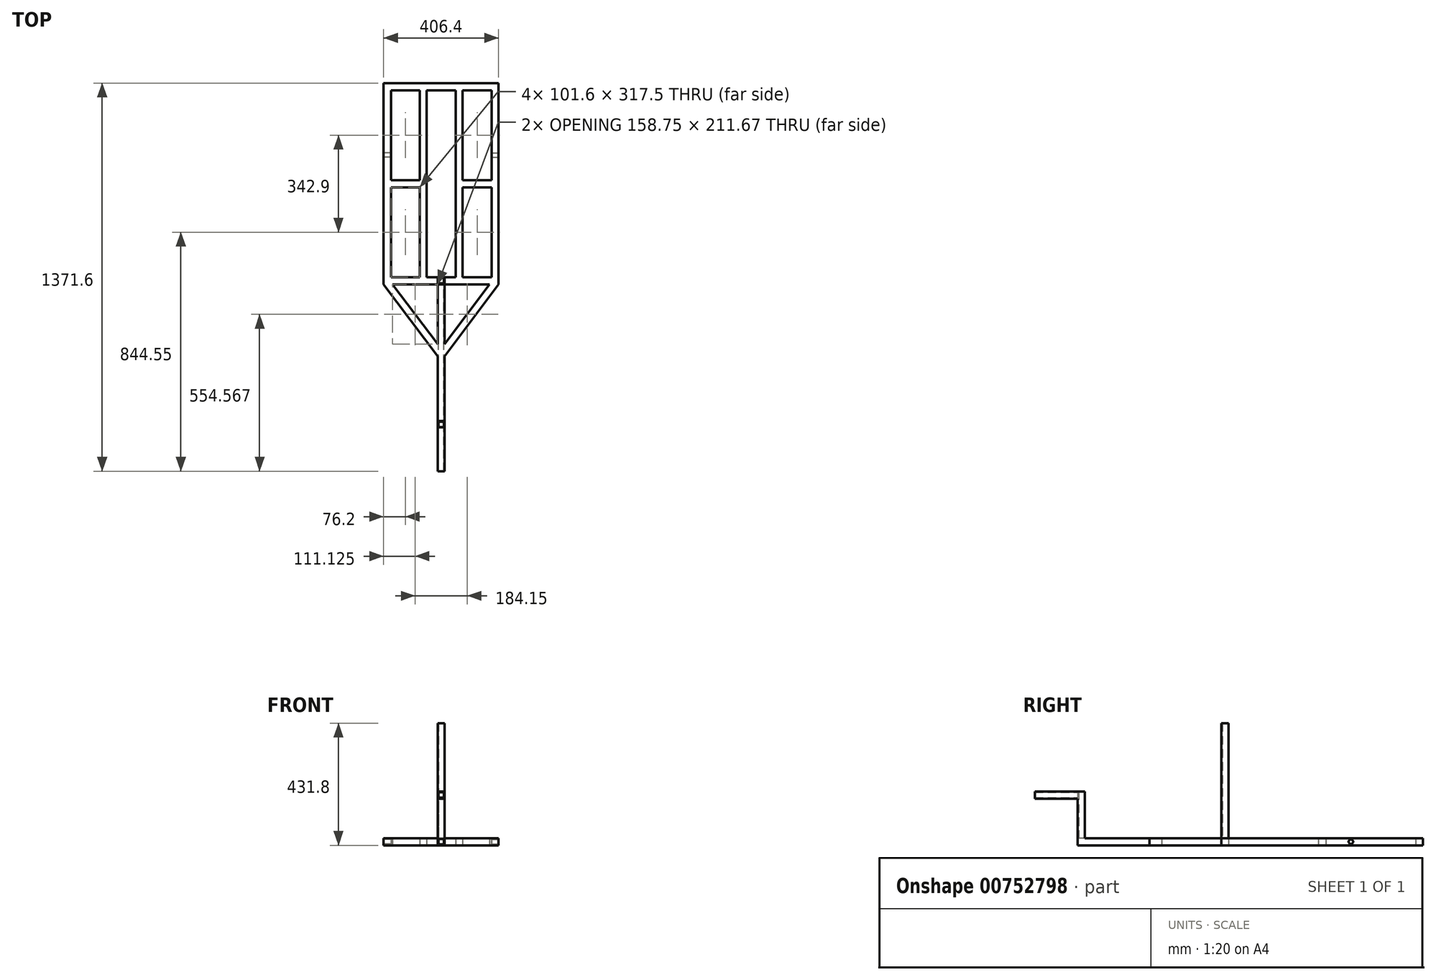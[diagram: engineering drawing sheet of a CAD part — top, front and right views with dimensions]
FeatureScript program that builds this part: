
annotation { "Feature Type Name" : "Feature", "Feature Type Description" : "" }
export const myFeature = defineFeature(function(context is Context, id is Id, definition is map)
    precondition{}
    {
        {
            var Q0;
            Q0=qCreatedBy(makeId("Top.planeOp"),FACE);
            var sketch = newSketch(context, id + "F0", { "sketchPlane" : qUnion([Q0])});
            skLineSegment(sketch, "E0.bottom", {"start": v(-203.2, 355.6) * mm, "end": v(203.2, 355.6) * mm});
            skLineSegment(sketch, "E0.top", {"start": v(-203.2, -355.6) * mm, "end": v(203.2, -355.6) * mm});
            skLineSegment(sketch, "E0.left", {"start": v(-203.2, 355.6) * mm, "end": v(-203.2, -355.6) * mm});
            skLineSegment(sketch, "E0.right", {"start": v(203.2, 355.6) * mm, "end": v(203.2, -355.6) * mm});
            skPoint(sketch, "E0.middle", {"position": v(0, 0) * mm});
            skLineSegment(sketch, "E1.bottom", {"start": v(177.8, 330.2) * mm, "end": v(76.2, 330.2) * mm});
            skLineSegment(sketch, "E1.top", {"start": v(177.8, -330.2) * mm, "end": v(76.2, -330.2) * mm});
            skLineSegment(sketch, "E1.left", {"start": v(177.8, 330.2) * mm, "end": v(177.8, 12.7) * mm});
            skLineSegment(sketch, "E1.right", {"start": v(-177.8, 330.2) * mm, "end": v(-177.8, 12.7) * mm});
            skLineSegment(sketch, "E2", {"start": v(-76.2, 330.2) * mm, "end": v(-76.2, 12.7) * mm});
            skLineSegment(sketch, "E3", {"start": v(-50.8, 330.2) * mm, "end": v(-50.8, -330.2) * mm});
            skLineSegment(sketch, "E4", {"start": v(50.8, 330.2) * mm, "end": v(50.8, -330.2) * mm});
            skLineSegment(sketch, "E5", {"start": v(76.2, 330.2) * mm, "end": v(76.2, 12.7) * mm});
            skLineSegment(sketch, "E6", {"start": v(-177.8, 12.7) * mm, "end": v(-76.2, 12.7) * mm});
            skLineSegment(sketch, "E7", {"start": v(-177.8, -12.7) * mm, "end": v(-76.2, -12.7) * mm});
            skLineSegment(sketch, "E8", {"start": v(76.2, 12.7) * mm, "end": v(177.8, 12.7) * mm});
            skLineSegment(sketch, "E9", {"start": v(76.2, -12.7) * mm, "end": v(177.8, -12.7) * mm});
            skLineSegment(sketch, "E10.trimOffspring", {"start": v(-177.8, -12.7) * mm, "end": v(-177.8, -330.2) * mm});
            skLineSegment(sketch, "E11.trimOffspring", {"start": v(-76.2, -12.7) * mm, "end": v(-76.2, -330.2) * mm});
            skLineSegment(sketch, "E12.trimOffspring", {"start": v(76.2, -12.7) * mm, "end": v(76.2, -330.2) * mm});
            skLineSegment(sketch, "E13.trimOffspring", {"start": v(177.8, -12.7) * mm, "end": v(177.8, -330.2) * mm});
            skLineSegment(sketch, "E14.trimOffspring", {"start": v(50.8, 330.2) * mm, "end": v(-50.8, 330.2) * mm});
            skLineSegment(sketch, "E15.trimOffspring", {"start": v(-76.2, 330.2) * mm, "end": v(-177.8, 330.2) * mm});
            skLineSegment(sketch, "E16.trimOffspring", {"start": v(-76.2, -330.2) * mm, "end": v(-177.8, -330.2) * mm});
            skLineSegment(sketch, "E17.trimOffspring", {"start": v(50.8, -330.2) * mm, "end": v(-50.8, -330.2) * mm});
            skSolve(sketch);
        }
        {
            var Q0;
            Q0=makeQuery(id+"F0.imprint","IMPRINT",FACE,{"disambiguationData":[TD([[makeQuery(id+"F0.imprint","IMPRINT",EDGE,{"derivedFrom":sQuery(id+"F0.wireOp",EDGE,"E0.bottom")}),-1.0]])]});
            extrude(context, id + "F1", {"entities" : qUnion([Q0]), "depth" : 25.4 * mm, "offsetDistance" : 25.4 * mm});
        }
        {
            var Q0;
            Q0=makeQuery(id+"F1.opExtrude","CAP_FACE",FACE,{"disambiguationData":[OSD([sQuery(id+"F0.wireOp",EDGE,"E0.bottom"),sQuery(id+"F0.wireOp",EDGE,"E0.top"),sQuery(id+"F0.wireOp",EDGE,"E0.left"),sQuery(id+"F0.wireOp",EDGE,"E0.right"),sQuery(id+"F0.wireOp",EDGE,"E1.bottom"),sQuery(id+"F0.wireOp",EDGE,"E1.top"),sQuery(id+"F0.wireOp",EDGE,"E1.left"),sQuery(id+"F0.wireOp",EDGE,"E1.right"),sQuery(id+"F0.wireOp",EDGE,"E2"),sQuery(id+"F0.wireOp",EDGE,"E3"),sQuery(id+"F0.wireOp",EDGE,"E4"),sQuery(id+"F0.wireOp",EDGE,"E5"),sQuery(id+"F0.wireOp",EDGE,"E6"),sQuery(id+"F0.wireOp",EDGE,"E7"),sQuery(id+"F0.wireOp",EDGE,"E8"),sQuery(id+"F0.wireOp",EDGE,"E9"),sQuery(id+"F0.wireOp",EDGE,"E10.trimOffspring"),sQuery(id+"F0.wireOp",EDGE,"E11.trimOffspring"),sQuery(id+"F0.wireOp",EDGE,"E12.trimOffspring"),sQuery(id+"F0.wireOp",EDGE,"E13.trimOffspring"),sQuery(id+"F0.wireOp",EDGE,"E14.trimOffspring"),sQuery(id+"F0.wireOp",EDGE,"E15.trimOffspring"),sQuery(id+"F0.wireOp",EDGE,"E16.trimOffspring"),sQuery(id+"F0.wireOp",EDGE,"E17.trimOffspring")])],"isStart":false});
            var sketch = newSketch(context, id + "F2", { "sketchPlane" : qUnion([Q0])});
            skLineSegment(sketch, "E18.bottom", {"start": v(12.7, -330.2) * mm, "end": v(-12.7, -330.2) * mm});
            skLineSegment(sketch, "E18.top", {"start": v(12.7, -355.6) * mm, "end": v(-12.7, -355.6) * mm});
            skLineSegment(sketch, "E18.left", {"start": v(12.7, -330.2) * mm, "end": v(12.7, -355.6) * mm});
            skLineSegment(sketch, "E18.right", {"start": v(-12.7, -330.2) * mm, "end": v(-12.7, -355.6) * mm});
            skPoint(sketch, "E18.middle", {"position": v(0, -342.9) * mm});
            skPoint(sketch, "E18.middle.positionSnap0", {"position": v(0, -355.6) * mm});
            skPoint(sketch, "E18.centerSnap0", {"position": v(0, -355.6) * mm});
            skLineSegment(sketch, "E19.bottom", {"start": v(9.53, -333.38) * mm, "end": v(-9.52, -333.38) * mm});
            skLineSegment(sketch, "E19.top", {"start": v(9.53, -352.43) * mm, "end": v(-9.52, -352.43) * mm});
            skLineSegment(sketch, "E19.left", {"start": v(9.53, -333.38) * mm, "end": v(9.53, -352.43) * mm});
            skLineSegment(sketch, "E19.right", {"start": v(-9.52, -333.38) * mm, "end": v(-9.52, -352.43) * mm});
            skSolve(sketch);
        }
        {
            var Q0;
            Q0=makeQuery(id+"F2.imprint","IMPRINT",FACE,{"disambiguationData":[TD([[makeQuery(id+"F2.imprint","IMPRINT",EDGE,{"derivedFrom":sQuery(id+"F2.wireOp",EDGE,"E18.bottom")}),1.0]])]});
            extrude(context, id + "F3", {"entities" : qUnion([Q0]), "operationType" : NewBodyOperationType.ADD, "depth" : 406.4 * mm, "offsetDistance" : 25.4 * mm});
        }
        {
            var Q0;
            Q0=makeQuery(id+"F1.opExtrude","SWEPT_FACE",FACE,{"disambiguationData":[OSD([sQuery(id+"F0.wireOp",EDGE,"E0.right")])]});
            var sketch = newSketch(context, id + "F4", { "sketchPlane" : qUnion([Q0])});
            skCircle(sketch, "E20", {"center": v(101.6, 12.7) * mm, "radius": 7.94 * mm});
            skSolve(sketch);
        }
        {
            var Q0;
            Q0 = qSketchRegion(id + "F4", true);
            extrude(context, id + "F5", {"entities" : qUnion([Q0]), "operationType" : NewBodyOperationType.REMOVE, "oppositeDirection" : true, "depth" : 25.4 * mm, "offsetDistance" : 25.4 * mm});
        }
        {
            var Q0;
            Q0=makeQuery(id+"F1.opExtrude","SWEPT_FACE",FACE,{"disambiguationData":[OSD([sQuery(id+"F0.wireOp",EDGE,"E0.left")])]});
            var sketch = newSketch(context, id + "F6", { "sketchPlane" : qUnion([Q0])});
            skCircle(sketch, "E21", {"center": v(-101.6, 12.7) * mm, "radius": 7.94 * mm});
            skSolve(sketch);
        }
        {
            var Q0;
            Q0=makeQuery(id+"F6.imprint","IMPRINT",FACE,{"disambiguationData":[TD([[makeQuery(id+"F6.imprint","IMPRINT",EDGE,{"derivedFrom":sQuery(id+"F6.wireOp",EDGE,"E21")}),1.0]])]});
            extrude(context, id + "F7", {"entities" : qUnion([Q0]), "operationType" : NewBodyOperationType.REMOVE, "oppositeDirection" : true, "depth" : 25.4 * mm, "offsetDistance" : 25.4 * mm});
        }
        {
            var Q0;
            Q0=makeQuery(id+"F3.boolean.opBoolean","MERGE",FACE,{"derivedFrom":[makeQuery(id+"F1.opExtrude","SWEPT_FACE",FACE,{"disambiguationData":[OSD([sQuery(id+"F0.wireOp",EDGE,"E0.top")])]}),makeQuery(id+"F3.opExtrude","SWEPT_FACE",FACE,{"disambiguationData":[OSD([sQuery(id+"F2.wireOp",EDGE,"E18.top")])]})]});
            var sketch = newSketch(context, id + "F8", { "sketchPlane" : qUnion([Q0])});
            skLineSegment(sketch, "E22.bottom", {"start": v(12.7, 25.4) * mm, "end": v(-12.7, 25.4) * mm});
            skLineSegment(sketch, "E22.top", {"start": v(12.7, 0) * mm, "end": v(-12.7, 0) * mm});
            skLineSegment(sketch, "E22.left", {"start": v(12.7, 25.4) * mm, "end": v(12.7, 0) * mm});
            skLineSegment(sketch, "E22.right", {"start": v(-12.7, 25.4) * mm, "end": v(-12.7, 0) * mm});
            skPoint(sketch, "E22.middle", {"position": v(0, 12.7) * mm});
            skLineSegment(sketch, "E23.bottom", {"start": v(9.52, 22.23) * mm, "end": v(-9.53, 22.23) * mm});
            skLineSegment(sketch, "E23.top", {"start": v(9.52, 3.17) * mm, "end": v(-9.53, 3.17) * mm});
            skLineSegment(sketch, "E23.left", {"start": v(9.52, 22.23) * mm, "end": v(9.52, 3.17) * mm});
            skLineSegment(sketch, "E23.right", {"start": v(-9.53, 22.23) * mm, "end": v(-9.53, 3.18) * mm});
            skSolve(sketch);
        }
        {
            var Q0;
            Q0=makeQuery(id+"F8.imprint","IMPRINT",FACE,{"disambiguationData":[TD([[makeQuery(id+"F8.imprint","IMPRINT",EDGE,{"derivedFrom":sQuery(id+"F8.wireOp",EDGE,"E22.bottom")}),1.0]])]});
            extrude(context, id + "F9", {"entities" : qUnion([Q0]), "operationType" : NewBodyOperationType.ADD, "depth" : 508 * mm, "offsetDistance" : 25.4 * mm});
        }
        {
            var Q0;
            Q0=makeQuery(id+"F9.opExtrude","SWEPT_FACE",FACE,{"disambiguationData":[OSD([sQuery(id+"F8.wireOp",EDGE,"E22.bottom")])]});
            var sketch = newSketch(context, id + "F10", { "sketchPlane" : qUnion([Q0])});
            skLineSegment(sketch, "E24.bottom", {"start": v(12.7, -838.2) * mm, "end": v(-12.7, -838.2) * mm});
            skLineSegment(sketch, "E24.top", {"start": v(12.7, -863.6) * mm, "end": v(-12.7, -863.6) * mm});
            skLineSegment(sketch, "E24.left", {"start": v(12.7, -838.2) * mm, "end": v(12.7, -863.6) * mm});
            skLineSegment(sketch, "E24.right", {"start": v(-12.7, -838.2) * mm, "end": v(-12.7, -863.6) * mm});
            skPoint(sketch, "E24.middle", {"position": v(0, -850.9) * mm});
            skLineSegment(sketch, "E25.0", {"start": v(9.52, -841.38) * mm, "end": v(-9.52, -841.38) * mm});
            skLineSegment(sketch, "E25.1", {"start": v(9.52, -841.38) * mm, "end": v(9.52, -860.42) * mm});
            skLineSegment(sketch, "E25.2", {"start": v(9.52, -860.42) * mm, "end": v(-9.52, -860.42) * mm});
            skLineSegment(sketch, "E25.3", {"start": v(-9.52, -841.38) * mm, "end": v(-9.52, -860.42) * mm});
            skLineSegment(sketch, "E26.0", {"start": v(19.05, -349.25) * mm, "end": v(-19.05, -349.25) * mm});
            skSolve(sketch);
        }
        {
            var Q0;
            Q0 = qSketchRegion(id + "F10", true);
            extrude(context, id + "F11", {"entities" : qUnion([Q0]), "operationType" : NewBodyOperationType.ADD, "depth" : 165.1 * mm, "offsetDistance" : 25.4 * mm});
        }
        {
            var Q0;
            Q0=makeQuery(id+"F11.boolean.opBoolean","MERGE",FACE,{"derivedFrom":[makeQuery(id+"F9.opExtrude","CAP_FACE",FACE,{"disambiguationData":[OSD([sQuery(id+"F8.wireOp",EDGE,"E22.bottom"),sQuery(id+"F8.wireOp",EDGE,"E22.top"),sQuery(id+"F8.wireOp",EDGE,"E22.left"),sQuery(id+"F8.wireOp",EDGE,"E22.right"),sQuery(id+"F8.wireOp",EDGE,"E23.bottom"),sQuery(id+"F8.wireOp",EDGE,"E23.top"),sQuery(id+"F8.wireOp",EDGE,"E23.left"),sQuery(id+"F8.wireOp",EDGE,"E23.right")])],"isStart":false}),makeQuery(id+"F11.opExtrude","SWEPT_FACE",FACE,{"disambiguationData":[OSD([sQuery(id+"F10.wireOp",EDGE,"E24.top")])]})]});
            var sketch = newSketch(context, id + "F12", { "sketchPlane" : qUnion([Q0])});
            skLineSegment(sketch, "E27.bottom", {"start": v(12.7, 190.5) * mm, "end": v(-12.7, 190.5) * mm});
            skLineSegment(sketch, "E27.top", {"start": v(12.7, 165.1) * mm, "end": v(-12.7, 165.1) * mm});
            skLineSegment(sketch, "E27.left", {"start": v(12.7, 190.5) * mm, "end": v(12.7, 165.1) * mm});
            skLineSegment(sketch, "E27.right", {"start": v(-12.7, 190.5) * mm, "end": v(-12.7, 165.1) * mm});
            skPoint(sketch, "E27.middle", {"position": v(0, 177.8) * mm});
            skLineSegment(sketch, "E28.bottom", {"start": v(9.53, 187.33) * mm, "end": v(-9.53, 187.33) * mm});
            skLineSegment(sketch, "E28.top", {"start": v(9.53, 168.28) * mm, "end": v(-9.53, 168.28) * mm});
            skLineSegment(sketch, "E28.left", {"start": v(9.53, 187.33) * mm, "end": v(9.53, 168.28) * mm});
            skLineSegment(sketch, "E28.right", {"start": v(-9.53, 187.33) * mm, "end": v(-9.53, 168.28) * mm});
            skSolve(sketch);
        }
        {
            var Q0;
            Q0 = qSketchRegion(id + "F12", true);
            extrude(context, id + "F13", {"entities" : qUnion([Q0]), "operationType" : NewBodyOperationType.ADD, "depth" : 152.4 * mm, "offsetDistance" : 25.4 * mm});
        }
        {
            var Q0;
            Q0=qCreatedBy(makeId("Top.planeOp"),FACE);
            var sketch = newSketch(context, id + "F14", { "sketchPlane" : qUnion([Q0])});
            skLineSegment(sketch, "E29", {"start": v(-203.2, -355.6) * mm, "end": v(-12.7, -609.6) * mm});
            skLineSegment(sketch, "E30", {"start": v(-171.45, -355.6) * mm, "end": v(-12.7, -567.27) * mm});
            skLineSegment(sketch, "E31.MirrorCS", {"start": v(203.2, -355.6) * mm, "end": v(12.7, -609.6) * mm});
            skLineSegment(sketch, "E32.MirrorCS", {"start": v(171.45, -355.6) * mm, "end": v(12.7, -567.27) * mm});
            skLineSegment(sketch, "E33", {"start": v(-203.2, -355.6) * mm, "end": v(-171.45, -355.6) * mm});
            skLineSegment(sketch, "E34", {"start": v(171.45, -355.6) * mm, "end": v(203.2, -355.6) * mm});
            skLineSegment(sketch, "E35", {"start": v(12.7, -609.6) * mm, "end": v(12.7, -567.27) * mm});
            skLineSegment(sketch, "E36", {"start": v(-12.7, -609.6) * mm, "end": v(-12.7, -567.27) * mm});
            skSolve(sketch);
        }
        {
            var Q0;
            Q0=makeQuery(id+"F14.imprint","IMPRINT",FACE,{"disambiguationData":[TD([[makeQuery(id+"F14.imprint","IMPRINT",EDGE,{"derivedFrom":sQuery(id+"F14.wireOp",EDGE,"E29")}),1.0]])]});
            var Q1;
            Q1=makeQuery(id+"F14.imprint","IMPRINT",FACE,{"disambiguationData":[TD([[makeQuery(id+"F14.imprint","IMPRINT",EDGE,{"derivedFrom":sQuery(id+"F14.wireOp",EDGE,"E31.MirrorCS")}),-1.0]])]});
            extrude(context, id + "F15", {"entities" : qUnion([Q0, Q1]), "operationType" : NewBodyOperationType.ADD, "depth" : 25.4 * mm, "offsetDistance" : 25.4 * mm});
        }
    });
